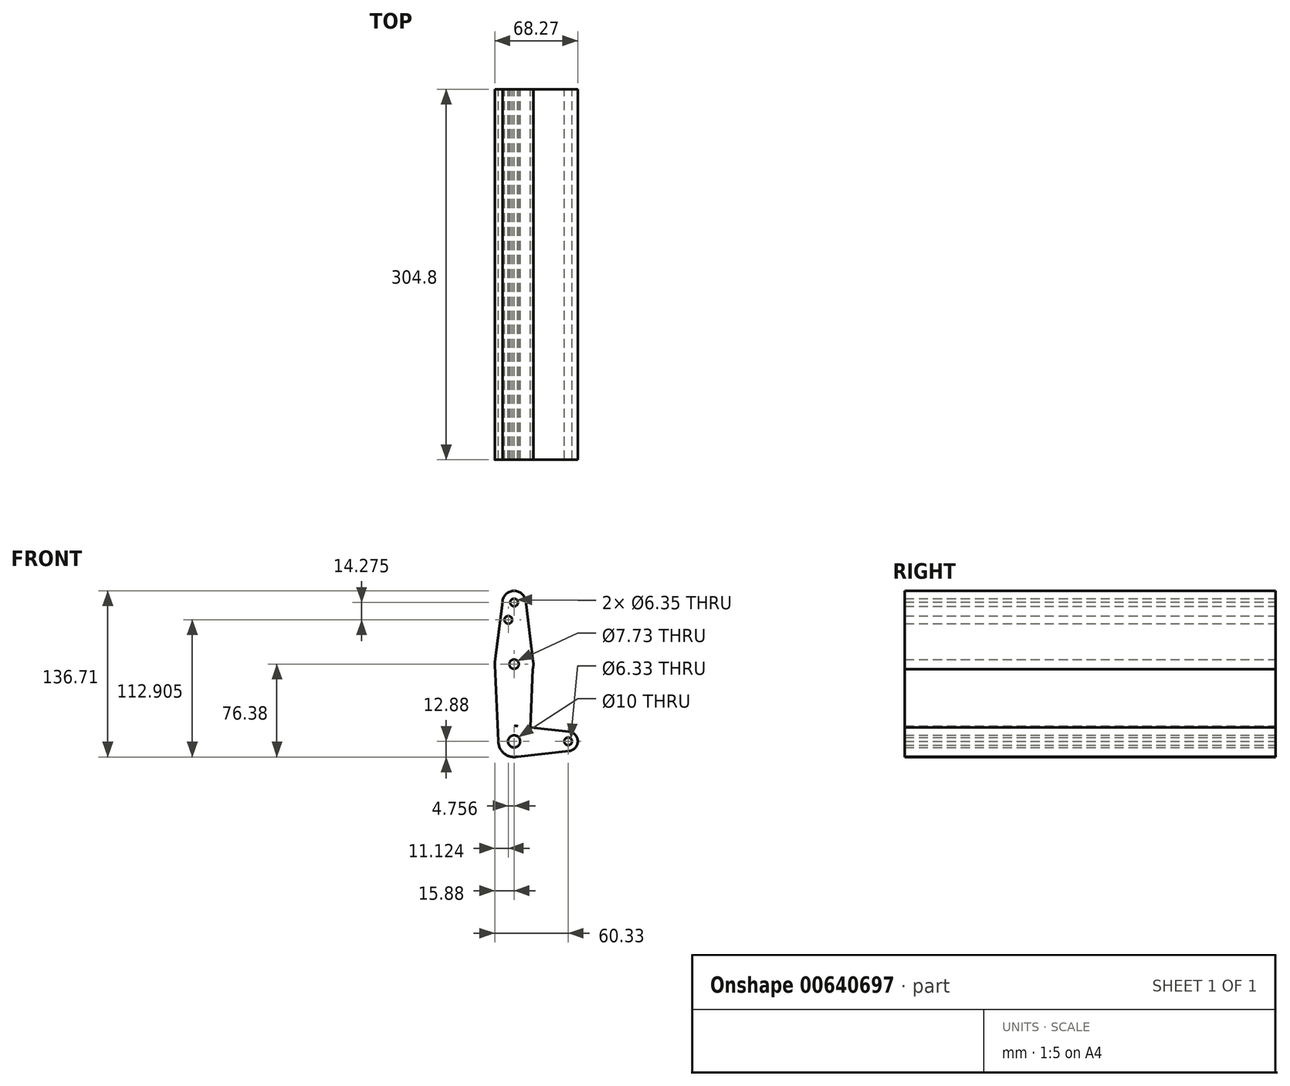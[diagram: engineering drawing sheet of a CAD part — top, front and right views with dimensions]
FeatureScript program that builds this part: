
annotation { "Feature Type Name" : "Feature", "Feature Type Description" : "" }
export const myFeature = defineFeature(function(context is Context, id is Id, definition is map)
    precondition{}
    {
        {
            var Q0;
            Q0=qCreatedBy(makeId("Front.planeOp"),FACE);
            var sketch = newSketch(context, id + "F0", { "sketchPlane" : qUnion([Q0])});
            skLineSegment(sketch, "E0", {"start": v(0, 0) * mm, "end": v(0, 114.3) * mm, "construction": true});
            skLineSegment(sketch, "E1", {"start": v(0, 0) * mm, "end": v(44.45, 0) * mm, "construction": true});
            skCircle(sketch, "E2", {"center": v(0, 0) * mm, "radius": 12.88 * mm});
            skCircle(sketch, "E3", {"center": v(0, 114.3) * mm, "radius": 9.53 * mm});
            skCircle(sketch, "E4", {"center": v(0, 63.5) * mm, "radius": 15.88 * mm});
            skCircle(sketch, "E5", {"center": v(44.45, 0) * mm, "radius": 7.94 * mm});
            skLineSegment(sketch, "E6", {"start": v(-9.52, 114.6) * mm, "end": v(-15.75, 65.5) * mm});
            skLineSegment(sketch, "E7", {"start": v(9.45, 115.52) * mm, "end": v(15.75, 65.5) * mm});
            skLineSegment(sketch, "E8", {"start": v(0, 12.88) * mm, "end": v(45.32, 7.89) * mm});
            skLineSegment(sketch, "E9", {"start": v(0, -12.88) * mm, "end": v(45.32, -7.89) * mm});
            skCircle(sketch, "E10", {"center": v(0, 114.3) * mm, "radius": 3.18 * mm});
            skCircle(sketch, "E11", {"center": v(-4.76, 100.03) * mm, "radius": 3.18 * mm});
            skCircle(sketch, "E12", {"center": v(0, 63.5) * mm, "radius": 3.87 * mm});
            skCircle(sketch, "E13", {"center": v(0, 0) * mm, "radius": 5 * mm});
            skCircle(sketch, "E14", {"center": v(44.45, 0) * mm, "radius": 3.17 * mm});
            skLineSegment(sketch, "E15", {"start": v(-12.88, 0) * mm, "end": v(-15.86, 62.75) * mm});
            skLineSegment(sketch, "E16", {"start": v(12.88, 0) * mm, "end": v(15.34, 59.4) * mm});
            skSolve(sketch);
        }
        {
            var Q0;
            Q0 = qSketchRegion(id + "F0", true);
            extrude(context, id + "F1", {"entities" : qUnion([Q0]), "depth" : 304.8 * mm, "offsetDistance" : 25.4 * mm});
        }
    });
